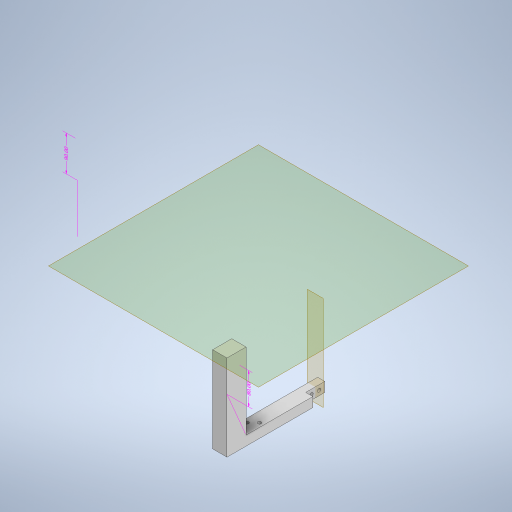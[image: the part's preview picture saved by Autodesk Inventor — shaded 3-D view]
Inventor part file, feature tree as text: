
AUTODESK INVENTOR PART (.ipt)
format: ipt  version: 2023 (Build 270158000, 158)  size: 384,512 bytes
history: native  units: mm
features: sketch x9, extrude x5, other x4, hole x3, plane x2, split x2
ambient origin geometry x8: Origin, YZ Plane, XZ Plane, XY Plane, X Axis, Y Axis, Z Axis, Center Point
bodies: Body1 (feature_tree), Body2 (feature_tree)
feature tree (25):
  other  "Sólido1"
  other  "Anotaciones"
  extrude  "Extrusión1"  Depth=15.0mm
  hole  "Agujero1"  [1 undecoded]
  extrude  "Extrusión2"  Depth=15.0mm
  extrude  "Extrusión3"  Depth=80.0mm TaperAngle=0.0deg
  extrude  "Extrusión4"  Depth=200.0mm
  extrude  "Extrusión5"  Depth=20.0mm
  hole  "Agujero2"  [1 undecoded]
  plane  "Plano de trabajo1"
  split  "Dividir1"
  sketch  "Boceto9"  dims[d37=20.0mm d38=20.0mm]
  plane  "Plano de trabajo2"
  hole  "Agujero3"  [1 undecoded]
  split  "Dividir2"
  sketch  "Boceto2"  dims[d7=15.0mm d8=200.0mm]
  sketch  "Boceto3"  dims[d9=10.0mm d10=0.0mm]
  sketch  "Boceto4"  dims[d12=1.75mm d13=1.75mm d14=1.75mm d15=1.75mm d16=10.0mm d17=10.0mm d19=30.0mm]
  sketch  "Boceto5"  dims[d20=3.5mm d21=6.0mm d22=4.0mm d23=2.0mm d24=90.0deg d25=8.0mm d26=20.594885mm d27=15.0mm]
  sketch  "Boceto6"  dims[d28=20.0mm d29=80.0mm d30=0.0mm]
  sketch  "Boceto7"  dims[d31=48.0mm d32=200.0mm]
  sketch  "Boceto8"  dims[d33=110.0mm d34=0.0mm d36=20.0mm]
  sketch  "Boceto10"  dims[d39=90.0mm d40=0.0mm d42=10.0mm d43=30.0mm d44=0.0mm d46=1.75mm d47=1.75mm d48=1.75mm d49=1.75mm d50=10.0mm d51=10.0mm d52=15.0mm d56=3.5mm d57=6.0mm d58=4.0mm d59=2.0mm d60=90.0deg d61=8.0mm d62=20.594885mm d63=10.0mm d65=10.0mm d66=10.0mm d67=31.75mm d70=15.0mm d74=200.0mm d78=20.0mm d82=90.0deg d83=10.0mm d84=10.0mm d85=3.5mm d86=4.0mm d87=5.0mm d88=3.5mm d89=6.0mm d90=4.0mm d91=2.0mm d92=90.0deg d93=8.0mm d94=20.594885mm d75=1.454734mm d76=6.982969mm d77=80.0mm d79=4.097996mm d80=1.406125mm d81=90.0mm]
  other  "Cota lineal 2"
  other  "Cota lineal 3"
note: 3 required parameter values undecoded (feature->parameter linkage not recoverable at this tier; creation-order binding heuristic only, values carry confidence <= 0.55)
